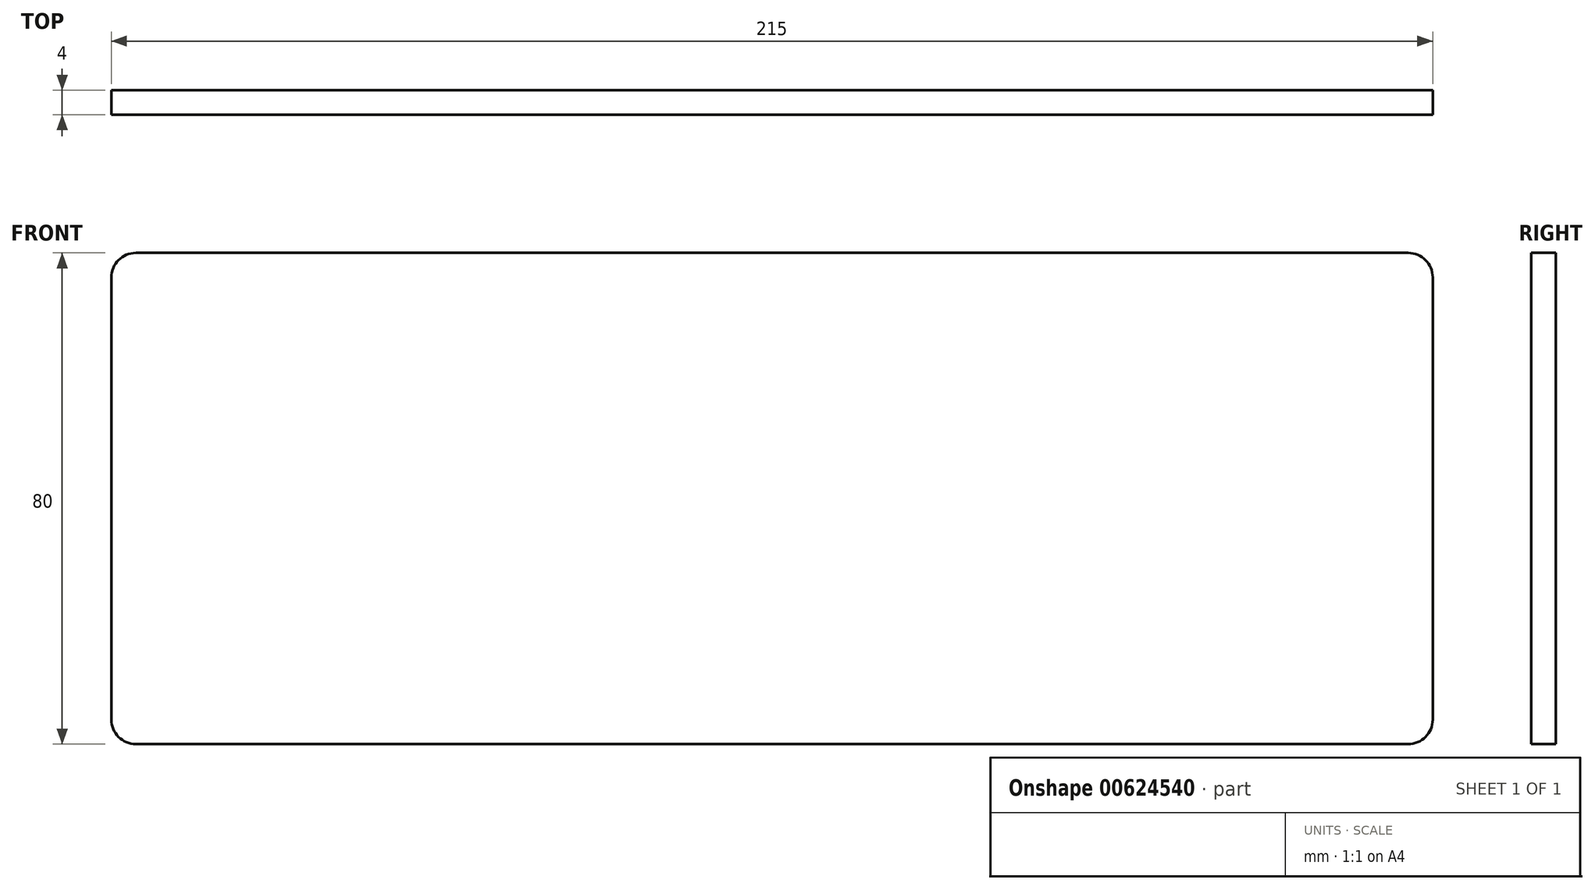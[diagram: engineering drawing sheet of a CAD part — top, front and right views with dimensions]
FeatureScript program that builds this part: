
annotation { "Feature Type Name" : "Feature", "Feature Type Description" : "" }
export const myFeature = defineFeature(function(context is Context, id is Id, definition is map)
    precondition{}
    {
        {
            var Q0;
            Q0=qCreatedBy(makeId("Front.planeOp"),FACE);
            var sketch = newSketch(context, id + "F0", { "sketchPlane" : qUnion([Q0])});
            skLineSegment(sketch, "E0.bottom", {"start": v(107.5, 40) * mm, "end": v(-107.5, 40) * mm});
            skLineSegment(sketch, "E0.top", {"start": v(107.5, -40) * mm, "end": v(-107.5, -40) * mm});
            skLineSegment(sketch, "E0.left", {"start": v(107.5, 40) * mm, "end": v(107.5, -40) * mm});
            skLineSegment(sketch, "E0.right", {"start": v(-107.5, 40) * mm, "end": v(-107.5, -40) * mm});
            skPoint(sketch, "E0.middle", {"position": v(0, 0) * mm});
            skSolve(sketch);
        }
        {
            var Q0;
            Q0 = qSketchRegion(id + "F0", true);
            extrude(context, id + "F1", {"entities" : qUnion([Q0]), "depth" : 4 * mm, "offsetDistance" : 25 * mm});
        }
        {
            var Q0;
            Q0=makeQuery(id+"F1.opExtrude","SWEPT_EDGE",EDGE,{"disambiguationData":[OSD([sQuery(id+"F0.wireOp",EDGE,"E0.bottom"),sQuery(id+"F0.wireOp",EDGE,"E0.left")])]});
            var Q1;
            Q1=makeQuery(id+"F1.opExtrude","SWEPT_EDGE",EDGE,{"disambiguationData":[OSD([sQuery(id+"F0.wireOp",EDGE,"E0.top"),sQuery(id+"F0.wireOp",EDGE,"E0.left")])]});
            var Q2;
            Q2=makeQuery(id+"F1.opExtrude","SWEPT_EDGE",EDGE,{"disambiguationData":[OSD([sQuery(id+"F0.wireOp",EDGE,"E0.top"),sQuery(id+"F0.wireOp",EDGE,"E0.right")])]});
            var Q3;
            Q3=makeQuery(id+"F1.opExtrude","SWEPT_EDGE",EDGE,{"disambiguationData":[OSD([sQuery(id+"F0.wireOp",EDGE,"E0.bottom"),sQuery(id+"F0.wireOp",EDGE,"E0.right")])]});
            fillet(context, id + "F2", {"entities" : qUnion([Q0, Q1, Q2, Q3]), "radius" : 4 * mm, "tangentPropagation" : true, "allowEdgeOverflow" : false});
        }
    });
